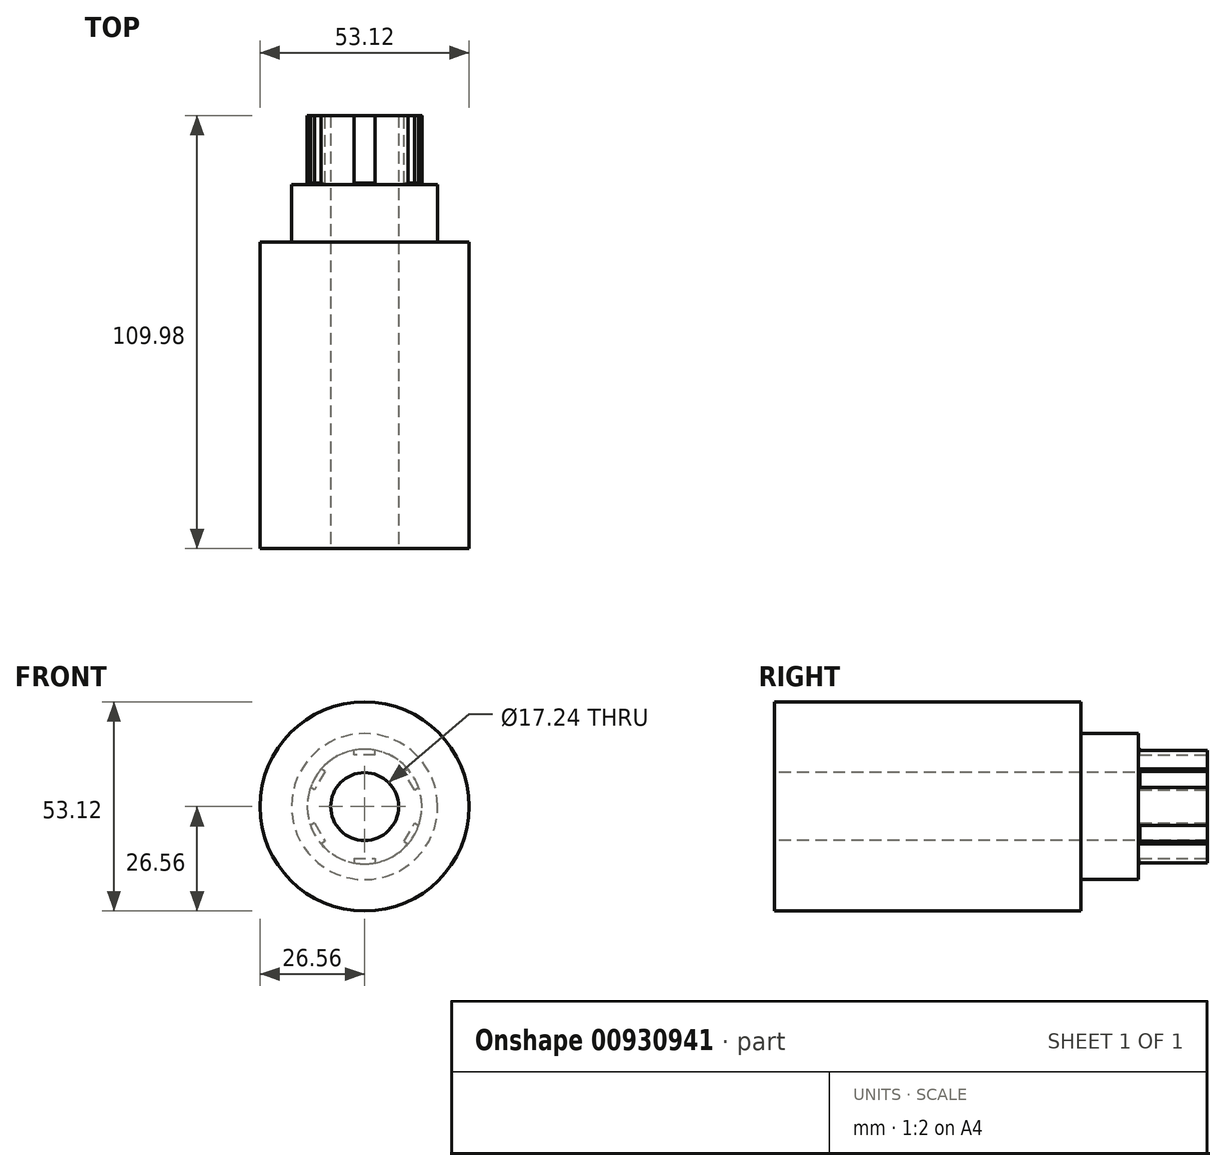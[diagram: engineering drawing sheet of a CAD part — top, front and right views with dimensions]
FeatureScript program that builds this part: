
annotation { "Feature Type Name" : "Feature", "Feature Type Description" : "" }
export const myFeature = defineFeature(function(context is Context, id is Id, definition is map)
    precondition{}
    {
        {
            var Q0;
            Q0=qCreatedBy(makeId("Right.planeOp"),FACE);
            var sketch = newSketch(context, id + "F0", { "sketchPlane" : qUnion([Q0])});
            skLineSegment(sketch, "E0", {"start": v(-59.98, 26.56) * mm, "end": v(17.87, 26.56) * mm});
            skLineSegment(sketch, "E1", {"start": v(17.87, 26.56) * mm, "end": v(17.87, 18.56) * mm});
            skLineSegment(sketch, "E2", {"start": v(17.87, 18.56) * mm, "end": v(32.5, 18.56) * mm});
            skLineSegment(sketch, "E3", {"start": v(32.5, 18.56) * mm, "end": v(32.5, 14.56) * mm});
            skLineSegment(sketch, "E4", {"start": v(32.5, 14.56) * mm, "end": v(50, 14.56) * mm});
            skLineSegment(sketch, "E5", {"start": v(50, 14.56) * mm, "end": v(50, 8.62) * mm});
            skLineSegment(sketch, "E6", {"start": v(-59.98, 8.62) * mm, "end": v(-59.98, 26.56) * mm});
            skLineSegment(sketch, "E7", {"start": v(-59.98, 8.62) * mm, "end": v(50, 8.62) * mm});
            skLineSegment(sketch, "E8", {"start": v(-62.58, 0) * mm, "end": v(64.8, 0) * mm, "construction": true});
            skSolve(sketch);
        }
        {
            var Q0;
            Q0 = qSketchRegion(id + "F0", true);
            var Q1;
            Q1=sQuery(id+"F0.wireOp",EDGE,"E8");
            revolve(context, id + "F1", {"surfaceOperationType" : NewSurfaceOperationType.NEW, "entities" : qUnion([Q0]), "axis" : qUnion([Q1]), "revolveType" : RevolveType.FULL});
        }
        {
            var Q0;
            Q0=makeQuery(id+"F1.opRevolve","SWEPT_FACE",FACE,{"disambiguationData":[OSD([sQuery(id+"F0.wireOp",EDGE,"E5")])]});
            var sketch = newSketch(context, id + "F2", { "sketchPlane" : qUnion([Q0])});
            skLineSegment(sketch, "E9", {"start": v(-2.72, 13.13) * mm, "end": v(-2.72, 14.56) * mm});
            skLineSegment(sketch, "E10", {"start": v(-2.72, 14.56) * mm, "end": v(0, 14.56) * mm});
            skLineSegment(sketch, "E11.MirrorCS", {"start": v(2.72, 14.56) * mm, "end": v(0, 14.56) * mm});
            skLineSegment(sketch, "E12.MirrorCS", {"start": v(2.72, 13.13) * mm, "end": v(2.72, 14.56) * mm});
            skLineSegment(sketch, "E13", {"start": v(-2.72, 13.13) * mm, "end": v(2.72, 13.13) * mm});
            skLineSegment(sketch, "E14.1.0", {"start": v(-12.73, 4.21) * mm, "end": v(-10.02, 8.92) * mm});
            skLineSegment(sketch, "E14.1.1", {"start": v(-10.02, 8.92) * mm, "end": v(-11.25, 9.63) * mm});
            skLineSegment(sketch, "E14.1.2", {"start": v(-11.25, 9.63) * mm, "end": v(-12.61, 7.28) * mm});
            skLineSegment(sketch, "E14.1.3", {"start": v(-13.97, 4.93) * mm, "end": v(-12.61, 7.28) * mm});
            skLineSegment(sketch, "E14.1.4", {"start": v(-12.73, 4.21) * mm, "end": v(-13.97, 4.93) * mm});
            skLineSegment(sketch, "E14.2.0", {"start": v(-10.02, -8.92) * mm, "end": v(-12.73, -4.21) * mm});
            skLineSegment(sketch, "E14.2.1", {"start": v(-12.73, -4.21) * mm, "end": v(-13.97, -4.93) * mm});
            skLineSegment(sketch, "E14.2.2", {"start": v(-13.97, -4.93) * mm, "end": v(-12.61, -7.28) * mm});
            skLineSegment(sketch, "E14.2.3", {"start": v(-11.25, -9.63) * mm, "end": v(-12.61, -7.28) * mm});
            skLineSegment(sketch, "E14.2.4", {"start": v(-10.02, -8.92) * mm, "end": v(-11.25, -9.63) * mm});
            skLineSegment(sketch, "E14.3.0", {"start": v(2.72, -13.13) * mm, "end": v(-2.72, -13.13) * mm});
            skLineSegment(sketch, "E14.3.1", {"start": v(-2.72, -13.13) * mm, "end": v(-2.72, -14.56) * mm});
            skLineSegment(sketch, "E14.3.2", {"start": v(-2.72, -14.56) * mm, "end": v(0, -14.56) * mm});
            skLineSegment(sketch, "E14.3.3", {"start": v(2.72, -14.56) * mm, "end": v(0, -14.56) * mm});
            skLineSegment(sketch, "E14.3.4", {"start": v(2.72, -13.13) * mm, "end": v(2.72, -14.56) * mm});
            skLineSegment(sketch, "E14.4.0", {"start": v(12.73, -4.21) * mm, "end": v(10.02, -8.92) * mm});
            skLineSegment(sketch, "E14.4.1", {"start": v(10.02, -8.92) * mm, "end": v(11.25, -9.63) * mm});
            skLineSegment(sketch, "E14.4.2", {"start": v(11.25, -9.63) * mm, "end": v(12.61, -7.28) * mm});
            skLineSegment(sketch, "E14.4.3", {"start": v(13.97, -4.93) * mm, "end": v(12.61, -7.28) * mm});
            skLineSegment(sketch, "E14.4.4", {"start": v(12.73, -4.21) * mm, "end": v(13.97, -4.93) * mm});
            skLineSegment(sketch, "E14.5.0", {"start": v(10.02, 8.92) * mm, "end": v(12.73, 4.21) * mm});
            skLineSegment(sketch, "E14.5.1", {"start": v(12.73, 4.21) * mm, "end": v(13.97, 4.93) * mm});
            skLineSegment(sketch, "E14.5.2", {"start": v(13.97, 4.93) * mm, "end": v(12.61, 7.28) * mm});
            skLineSegment(sketch, "E14.5.3", {"start": v(11.25, 9.63) * mm, "end": v(12.61, 7.28) * mm});
            skLineSegment(sketch, "E14.5.4", {"start": v(10.02, 8.92) * mm, "end": v(11.25, 9.63) * mm});
            skPoint(sketch, "E14.center", {"position": v(0, 0) * mm});
            skSolve(sketch);
        }
        {
            var Q0;
            {var subQ0=sQuery(id+"F2.wireOp",EDGE,"E10");Q0=makeQuery(id+"F2.imprint","IMPRINT",FACE,{"disambiguationData":[TD([[makeQuery(id+"F2.imprint","IMPRINT",EDGE,{"derivedFrom":subQ0}),-1.0]])]});}
            var Q1;
            {var subQ0=sQuery(id+"F2.wireOp",EDGE,"E11.MirrorCS");Q1=makeQuery(id+"F2.imprint","IMPRINT",FACE,{"disambiguationData":[TD([[makeQuery(id+"F2.imprint","IMPRINT",EDGE,{"derivedFrom":subQ0}),1.0]])]});}
            var Q2;
            {var subQ0=sQuery(id+"F2.wireOp",EDGE,"E14.1.2");Q2=makeQuery(id+"F2.imprint","IMPRINT",FACE,{"disambiguationData":[TD([[makeQuery(id+"F2.imprint","IMPRINT",EDGE,{"derivedFrom":subQ0}),1.0]])]});}
            var Q3;
            {var subQ0=sQuery(id+"F2.wireOp",EDGE,"E14.1.3");Q3=makeQuery(id+"F2.imprint","IMPRINT",FACE,{"disambiguationData":[TD([[makeQuery(id+"F2.imprint","IMPRINT",EDGE,{"derivedFrom":subQ0}),-1.0]])]});}
            var Q4;
            {var subQ0=sQuery(id+"F2.wireOp",EDGE,"E14.2.2");Q4=makeQuery(id+"F2.imprint","IMPRINT",FACE,{"disambiguationData":[TD([[makeQuery(id+"F2.imprint","IMPRINT",EDGE,{"derivedFrom":subQ0}),1.0]])]});}
            var Q5;
            {var subQ0=sQuery(id+"F2.wireOp",EDGE,"E14.2.3");Q5=makeQuery(id+"F2.imprint","IMPRINT",FACE,{"disambiguationData":[TD([[makeQuery(id+"F2.imprint","IMPRINT",EDGE,{"derivedFrom":subQ0}),-1.0]])]});}
            var Q6;
            {var subQ0=sQuery(id+"F2.wireOp",EDGE,"E14.3.2");Q6=makeQuery(id+"F2.imprint","IMPRINT",FACE,{"disambiguationData":[TD([[makeQuery(id+"F2.imprint","IMPRINT",EDGE,{"derivedFrom":subQ0}),1.0]])]});}
            var Q7;
            {var subQ0=sQuery(id+"F2.wireOp",EDGE,"E14.3.3");Q7=makeQuery(id+"F2.imprint","IMPRINT",FACE,{"disambiguationData":[TD([[makeQuery(id+"F2.imprint","IMPRINT",EDGE,{"derivedFrom":subQ0}),-1.0]])]});}
            var Q8;
            {var subQ0=sQuery(id+"F2.wireOp",EDGE,"E14.4.2");Q8=makeQuery(id+"F2.imprint","IMPRINT",FACE,{"disambiguationData":[TD([[makeQuery(id+"F2.imprint","IMPRINT",EDGE,{"derivedFrom":subQ0}),1.0]])]});}
            var Q9;
            {var subQ0=sQuery(id+"F2.wireOp",EDGE,"E14.4.3");Q9=makeQuery(id+"F2.imprint","IMPRINT",FACE,{"disambiguationData":[TD([[makeQuery(id+"F2.imprint","IMPRINT",EDGE,{"derivedFrom":subQ0}),-1.0]])]});}
            var Q10;
            {var subQ0=sQuery(id+"F2.wireOp",EDGE,"E14.5.2");Q10=makeQuery(id+"F2.imprint","IMPRINT",FACE,{"disambiguationData":[TD([[makeQuery(id+"F2.imprint","IMPRINT",EDGE,{"derivedFrom":subQ0}),1.0]])]});}
            var Q11;
            {var subQ0=sQuery(id+"F2.wireOp",EDGE,"E14.5.3");Q11=makeQuery(id+"F2.imprint","IMPRINT",FACE,{"disambiguationData":[TD([[makeQuery(id+"F2.imprint","IMPRINT",EDGE,{"derivedFrom":subQ0}),-1.0]])]});}
            var Q12;
            {var subQ4=sQuery(id+"F2.wireOp",EDGE,"E13");Q12=makeQuery(id+"F2.imprint","IMPRINT",FACE,{"disambiguationData":[TD([[makeQuery(id+"F2.imprint","IMPRINT",EDGE,{"derivedFrom":subQ4}),1.0]])]});}
            var Q13;
            {var subQ4=sQuery(id+"F2.wireOp",EDGE,"E14.2.0");Q13=makeQuery(id+"F2.imprint","IMPRINT",FACE,{"disambiguationData":[TD([[makeQuery(id+"F2.imprint","IMPRINT",EDGE,{"derivedFrom":subQ4}),1.0]])]});}
            var Q14;
            {var subQ4=sQuery(id+"F2.wireOp",EDGE,"E14.3.0");Q14=makeQuery(id+"F2.imprint","IMPRINT",FACE,{"disambiguationData":[TD([[makeQuery(id+"F2.imprint","IMPRINT",EDGE,{"derivedFrom":subQ4}),1.0]])]});}
            var Q15;
            {var subQ4=sQuery(id+"F2.wireOp",EDGE,"E14.4.0");Q15=makeQuery(id+"F2.imprint","IMPRINT",FACE,{"disambiguationData":[TD([[makeQuery(id+"F2.imprint","IMPRINT",EDGE,{"derivedFrom":subQ4}),1.0]])]});}
            var Q16;
            {var subQ4=sQuery(id+"F2.wireOp",EDGE,"E14.5.0");Q16=makeQuery(id+"F2.imprint","IMPRINT",FACE,{"disambiguationData":[TD([[makeQuery(id+"F2.imprint","IMPRINT",EDGE,{"derivedFrom":subQ4}),1.0]])]});}
            var Q17;
            {var subQ5=sQuery(id+"F2.wireOp",EDGE,"E14.1.0");Q17=makeQuery(id+"F2.imprint","IMPRINT",FACE,{"disambiguationData":[TD([[makeQuery(id+"F2.imprint","IMPRINT",EDGE,{"derivedFrom":subQ5}),1.0]])]});}
            extrude(context, id + "F3", {"entities" : qUnion([Q0, Q1, Q2, Q3, Q4, Q5, Q6, Q7, Q8, Q9, Q10, Q11, Q12, Q13, Q14, Q15, Q16, Q17]), "oppositeDirection" : true, "depth" : 17.1 * mm, "offsetDistance" : 25 * mm});
        }
        {
            var Q0;
            Q0=makeQuery(id+"F3.opExtrude","SWEPT_BODY",BODY,{"disambiguationData":[OSD([sQuery(id+"F0.wireOp",EDGE,"E4"),sQuery(id+"F0.wireOp",EDGE,"E5"),sQuery(id+"F2.wireOp",EDGE,"E14.1.1"),sQuery(id+"F2.wireOp",EDGE,"E14.1.2")])]});
            var Q1;
            Q1=makeQuery(id+"F3.opExtrude","SWEPT_BODY",BODY,{"disambiguationData":[OSD([sQuery(id+"F0.wireOp",EDGE,"E4"),sQuery(id+"F0.wireOp",EDGE,"E5"),sQuery(id+"F2.wireOp",EDGE,"E14.1.3"),sQuery(id+"F2.wireOp",EDGE,"E14.1.4")])]});
            var Q2;
            Q2=makeQuery(id+"F3.opExtrude","SWEPT_BODY",BODY,{"disambiguationData":[OSD([sQuery(id+"F2.wireOp",EDGE,"E9"),sQuery(id+"F2.wireOp",EDGE,"E10"),sQuery(id+"F2.wireOp",EDGE,"E11.MirrorCS"),sQuery(id+"F2.wireOp",EDGE,"E12.MirrorCS"),sQuery(id+"F2.wireOp",EDGE,"E13")])]});
            var Q3;
            Q3=makeQuery(id+"F3.opExtrude","SWEPT_BODY",BODY,{"disambiguationData":[OSD([sQuery(id+"F2.wireOp",EDGE,"E14.5.0"),sQuery(id+"F2.wireOp",EDGE,"E14.5.1"),sQuery(id+"F2.wireOp",EDGE,"E14.5.2"),sQuery(id+"F2.wireOp",EDGE,"E14.5.3"),sQuery(id+"F2.wireOp",EDGE,"E14.5.4")])]});
            var Q4;
            Q4=makeQuery(id+"F3.opExtrude","SWEPT_BODY",BODY,{"disambiguationData":[OSD([sQuery(id+"F2.wireOp",EDGE,"E14.4.0"),sQuery(id+"F2.wireOp",EDGE,"E14.4.1"),sQuery(id+"F2.wireOp",EDGE,"E14.4.2"),sQuery(id+"F2.wireOp",EDGE,"E14.4.3"),sQuery(id+"F2.wireOp",EDGE,"E14.4.4")])]});
            var Q5;
            Q5=makeQuery(id+"F3.opExtrude","SWEPT_BODY",BODY,{"disambiguationData":[OSD([sQuery(id+"F2.wireOp",EDGE,"E14.3.0"),sQuery(id+"F2.wireOp",EDGE,"E14.3.1"),sQuery(id+"F2.wireOp",EDGE,"E14.3.2"),sQuery(id+"F2.wireOp",EDGE,"E14.3.3"),sQuery(id+"F2.wireOp",EDGE,"E14.3.4")])]});
            var Q6;
            Q6=makeQuery(id+"F3.opExtrude","SWEPT_BODY",BODY,{"disambiguationData":[OSD([sQuery(id+"F2.wireOp",EDGE,"E14.2.0"),sQuery(id+"F2.wireOp",EDGE,"E14.2.1"),sQuery(id+"F2.wireOp",EDGE,"E14.2.2"),sQuery(id+"F2.wireOp",EDGE,"E14.2.3"),sQuery(id+"F2.wireOp",EDGE,"E14.2.4")])]});
            var Q7;
            Q7=makeQuery(id+"F1.opRevolve","SWEPT_BODY",BODY,{"disambiguationData":[OSD([sQuery(id+"F0.wireOp",EDGE,"E0"),sQuery(id+"F0.wireOp",EDGE,"E1"),sQuery(id+"F0.wireOp",EDGE,"E2"),sQuery(id+"F0.wireOp",EDGE,"E3"),sQuery(id+"F0.wireOp",EDGE,"E4"),sQuery(id+"F0.wireOp",EDGE,"E5"),sQuery(id+"F0.wireOp",EDGE,"E6"),sQuery(id+"F0.wireOp",EDGE,"E7")])]});
            booleanBodies(context, id + "F4", {"operationType" : BooleanOperationType.SUBTRACTION, "tools" : qUnion([Q0, Q1, Q2, Q3, Q4, Q5, Q6]), "targets" : qUnion([Q7])});
        }
    });
